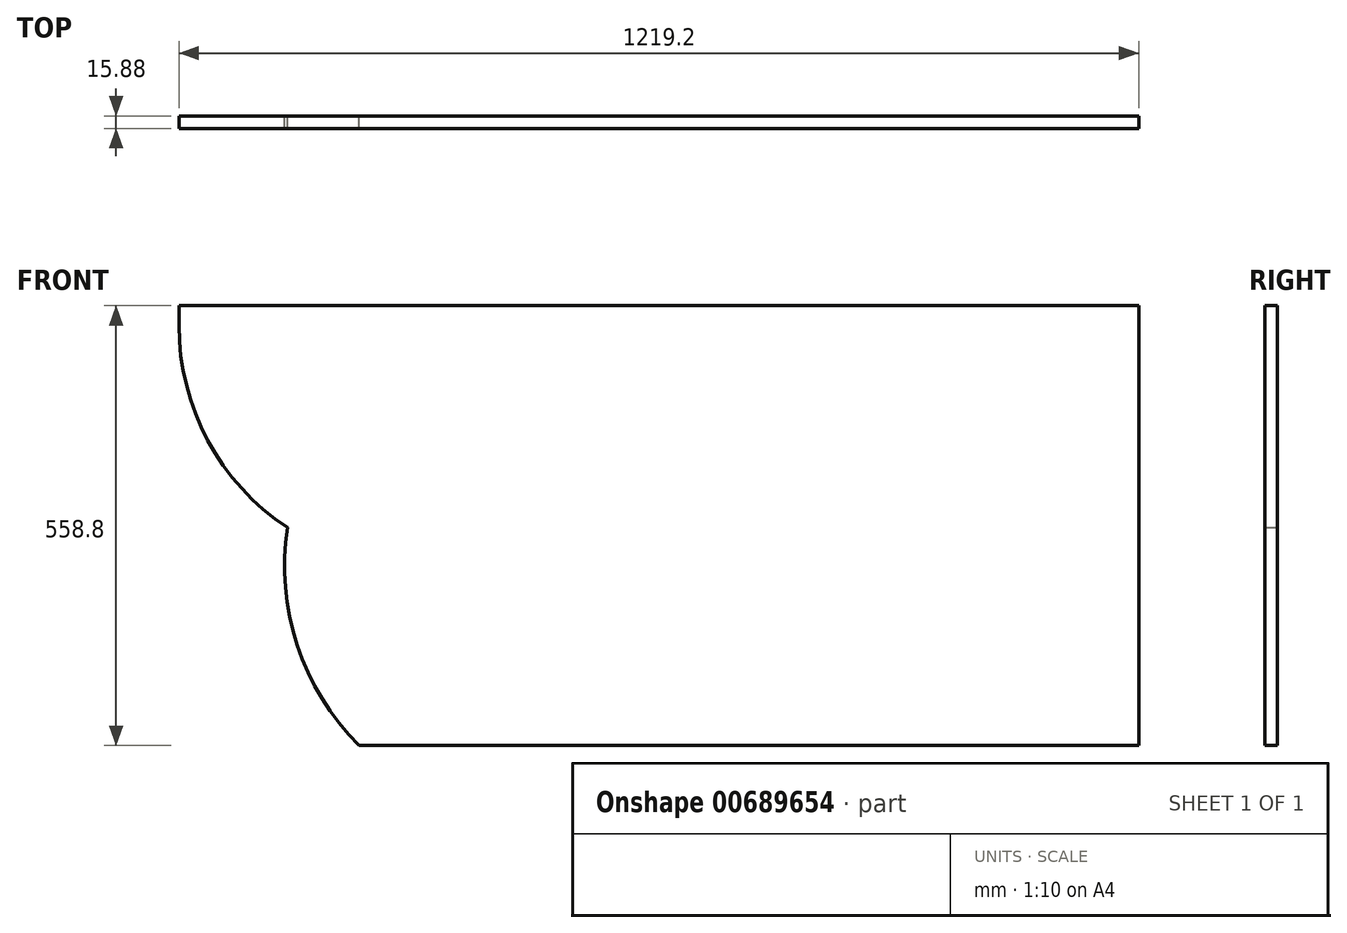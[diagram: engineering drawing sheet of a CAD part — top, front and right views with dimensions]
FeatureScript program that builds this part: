
annotation { "Feature Type Name" : "Feature", "Feature Type Description" : "" }
export const myFeature = defineFeature(function(context is Context, id is Id, definition is map)
    precondition{}
    {
        {
            var Q0;
            Q0=qCreatedBy(makeId("Front.planeOp"),FACE);
            var sketch = newSketch(context, id + "F0", { "sketchPlane" : qUnion([Q0])});
            skLineSegment(sketch, "E0", {"start": v(-68.54, -55.06) * mm, "end": v(1150.66, -55.06) * mm});
            skLineSegment(sketch, "E1", {"start": v(1150.66, -55.06) * mm, "end": v(1150.66, -613.86) * mm});
            skLineSegment(sketch, "E2", {"start": v(1150.66, -613.86) * mm, "end": v(160.06, -613.86) * mm});
            skLineSegment(sketch, "E3", {"start": v(-68.54, -55.06) * mm, "end": v(-68.54, -80.46) * mm});
            skArc(sketch, "E4", {"start": v(-68.54, -80.46) * mm, "mid": v(-31.96, -226.1) * mm, "end": v(69.1, -337.15) * mm});
            skArc(sketch, "E5", {"start": v(69.1, -337.15) * mm, "mid": v(81.78, -486.29) * mm, "end": v(160.06, -613.86) * mm});
            skPoint(sketch, "E6.start.orphan", {"position": v(45.76, -347.16) * mm});
            skSolve(sketch);
        }
        {
            var Q0;
            Q0=makeQuery(id+"F0.imprint","IMPRINT",FACE,{"disambiguationData":[TD([[makeQuery(id+"F0.imprint","IMPRINT",EDGE,{"derivedFrom":sQuery(id+"F0.wireOp",EDGE,"E0")}),-1.0]])]});
            extrude(context, id + "F1", {"entities" : qUnion([Q0]), "depth" : 15.88 * mm, "offsetDistance" : 25.4 * mm});
        }
    });
